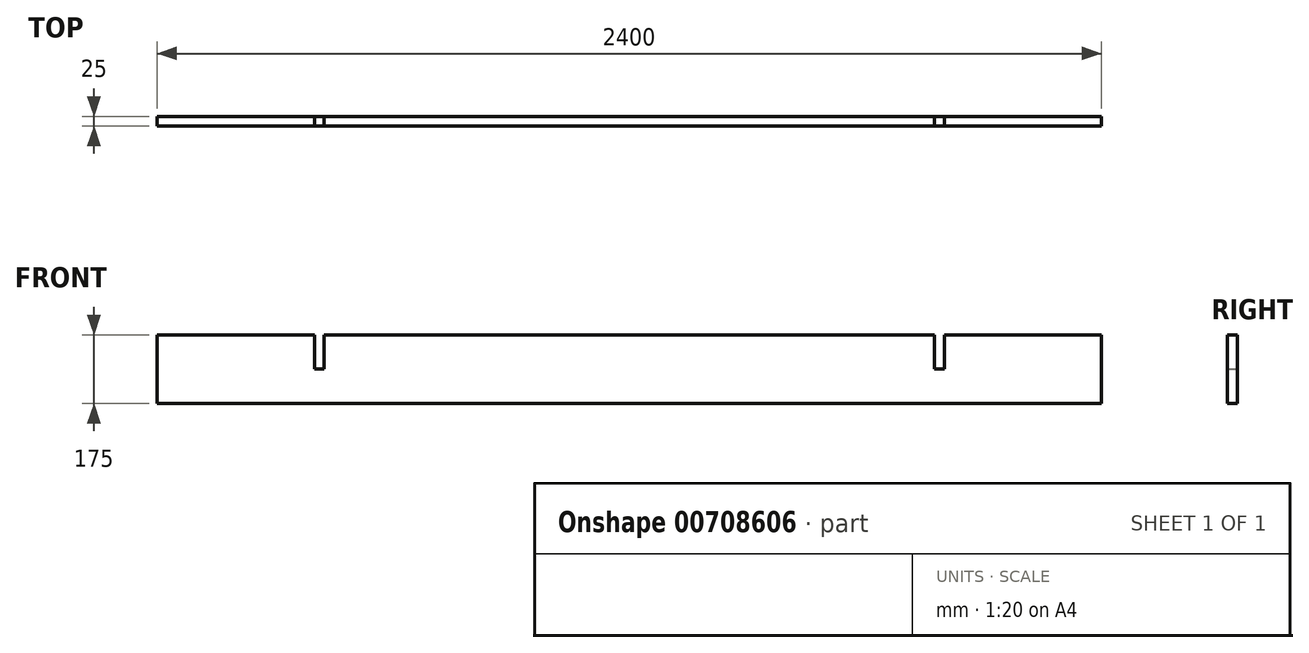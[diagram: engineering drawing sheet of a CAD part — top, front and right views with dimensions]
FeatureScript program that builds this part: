
annotation { "Feature Type Name" : "Feature", "Feature Type Description" : "" }
export const myFeature = defineFeature(function(context is Context, id is Id, definition is map)
    precondition{}
    {
        {
            assignVariable(context, id + "F0", {"name" : "Brett", "anyValue" : 25});
        }
        {
            var Q0;
            Q0=qCreatedBy(makeId("Front.planeOp"),FACE);
            var sketch = newSketch(context, id + "F1", { "sketchPlane" : qUnion([Q0])});
            skLineSegment(sketch, "E0", {"start": v(0, 0) * mm, "end": v(2400, 0) * mm});
            skLineSegment(sketch, "E1", {"start": v(2400, 0) * mm, "end": v(2400, 175) * mm});
            skLineSegment(sketch, "E2", {"start": v(2400, 175) * mm, "end": v(2000, 175) * mm});
            skLineSegment(sketch, "E3", {"start": v(2000, 175) * mm, "end": v(2000, 87.5) * mm});
            skLineSegment(sketch, "E4", {"start": v(2000, 87.5) * mm, "end": v(1975, 87.5) * mm});
            skLineSegment(sketch, "E5", {"start": v(1975, 87.5) * mm, "end": v(1975, 175) * mm});
            skLineSegment(sketch, "E6", {"start": v(1975, 175) * mm, "end": v(425, 175) * mm});
            skLineSegment(sketch, "E7", {"start": v(425, 175) * mm, "end": v(425, 87.5) * mm});
            skLineSegment(sketch, "E8", {"start": v(425, 87.5) * mm, "end": v(400, 87.5) * mm});
            skLineSegment(sketch, "E9", {"start": v(400, 87.5) * mm, "end": v(400, 175) * mm});
            skLineSegment(sketch, "E10", {"start": v(400, 175) * mm, "end": v(0, 175) * mm});
            skLineSegment(sketch, "E11", {"start": v(0, 175) * mm, "end": v(0, 0) * mm});
            skSolve(sketch);
        }
        {
            var Q0;
            Q0=makeQuery(id+"F1.imprint","IMPRINT",FACE,{"disambiguationData":[TD([[makeQuery(id+"F1.imprint","IMPRINT",EDGE,{"derivedFrom":sQuery(id+"F1.wireOp",EDGE,"E0")}),1.0]])]});
            extrude(context, id + "F2", {"entities" : qUnion([Q0]), "depth" : (getVariable(context, 'Brett')) * mm, "offsetDistance" : 25 * mm});
        }
    });
